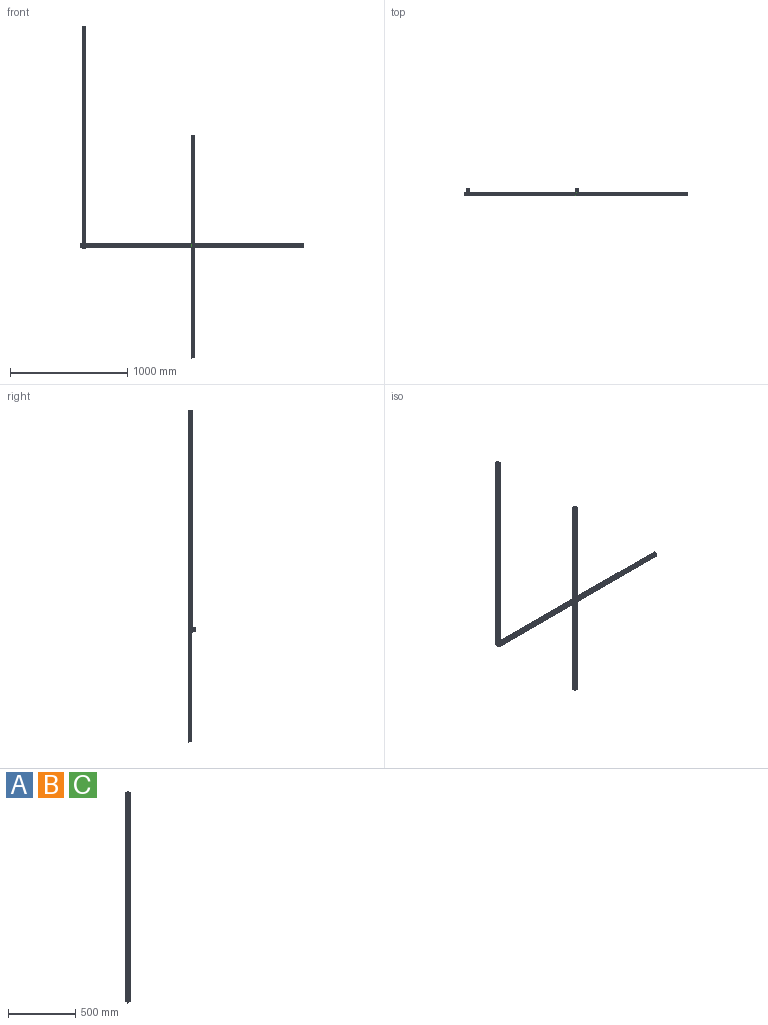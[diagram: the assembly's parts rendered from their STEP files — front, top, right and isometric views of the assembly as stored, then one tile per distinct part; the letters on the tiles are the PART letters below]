
ASSEMBLY  parts=3 mates=2
PART A: 242 faces, bbox 30x30x1900 mm
  f0: cylinder r=3.65mm len=1865.78mm, axis (0,0,1), area 6178.5mm2, adj f25,f39,f211,f240
  f1: cylinder r=3.65mm len=1865.78mm, axis (0,0,1), area 6178.5mm2, adj f31,f33,f212,f241
  f2: cylinder r=0.2mm len=1865.05mm, axis (0,0,1), area 193.9mm2, adj f3,f119,f212,f241
  f3: plane 1864.99x0.76mm, normal (-0.5,-0.87,0), area 1621.1mm2, adj f2,f4,f212,f241
  f4: cylinder r=0.2mm len=1864.7mm, axis (0,0,1), area 387.8mm2, adj f3,f123,f212,f241
  f5: plane 12.5x0.76mm, normal (0.5,-0.87,0), area 10.8mm2, adj f122,f124,f208,f212
  f6: cylinder r=0.2mm len=1865.05mm, axis (0,0,1), area 193.9mm2, adj f123,f125,f212,f241
  f7: cylinder r=0.2mm len=1865.05mm, axis (0,0,1), area 193.9mm2, adj f187,f189,f211,f240
  f8: plane 12.5x0.76mm, normal (0.5,0.87,0), area 10.8mm2, adj f188,f190,f208,f211
  f9: cylinder r=0.2mm len=1864.7mm, axis (0,0,1), area 387.8mm2, adj f10,f189,f211,f240
  f10: plane 1864.99x0.76mm, normal (-0.5,0.87,0), area 1621.1mm2, adj f9,f11,f211,f240
  f11: cylinder r=0.2mm len=1865.05mm, axis (0,0,1), area 193.9mm2, adj f10,f193,f211,f240
  f12: cylinder r=3.65mm len=1805.78mm, axis (0,0,1), area 5979.8mm2, adj f27,f29,f210,f239
  f13: cylinder r=3.65mm len=1805.78mm, axis (0,0,1), area 5979.8mm2, adj f35,f37,f209,f238
  f14: cylinder r=0.2mm len=1805.05mm, axis (0,0,1), area 187.7mm2, adj f15,f85,f210,f239
  f15: plane 1804.99x0.76mm, normal (0.87,-0.5,0), area 1569mm2, adj f14,f16,f210,f239
  f16: cylinder r=0.2mm len=1804.7mm, axis (0,0,1), area 375.3mm2, adj f15,f89,f210,f239
  f17: plane 42.5x0.76mm, normal (0.87,0.5,0), area 36.9mm2, adj f88,f90,f208,f210
  f18: cylinder r=0.2mm len=1805.05mm, axis (0,0,1), area 187.7mm2, adj f89,f91,f210,f239
  f19: cylinder r=0.2mm len=1805.05mm, axis (0,0,1), area 187.7mm2, adj f153,f155,f209,f238
  f20: plane 42.5x0.76mm, normal (-0.87,0.5,0), area 36.9mm2, adj f154,f156,f208,f209
  f21: cylinder r=0.2mm len=1804.7mm, axis (0,0,1), area 375.3mm2, adj f22,f155,f209,f238
  f22: plane 1804.99x0.76mm, normal (-0.87,-0.5,0), area 1569mm2, adj f21,f23,f209,f238
  f23: cylinder r=0.2mm len=1805.05mm, axis (0,0,1), area 187.7mm2, adj f22,f159,f209,f238
  f24: cylinder r=3.65mm len=12.89mm, axis (0,0,1), area 41.5mm2, adj f25,f39,f208,f211
  f25: plane 1900x1.54mm, normal (0.63,-0.78,0), area 3739.9mm2, adj f0,f24,f26,f208,f211,f217,f237,f240
  f26: cylinder r=5.5mm len=1900mm, axis (0,0,1), area 3691.1mm2, adj f25,f27,f208,f237
  f27: plane 1900x1.55mm, normal (-0.79,0.62,0), area 3752.3mm2, adj f12,f26,f28,f208,f210,f218,f237,f239
  f28: cylinder r=3.65mm len=42.89mm, axis (0,0,1), area 140.9mm2, adj f27,f29,f208,f210
  f29: plane 1900x1.55mm, normal (-0.79,-0.62,0), area 3752.3mm2, adj f12,f28,f30,f208,f210,f218,f237,f239
  f30: cylinder r=5.5mm len=1900mm, axis (0,0,1), area 3691.1mm2, adj f29,f31,f208,f237
  f31: plane 1900x1.54mm, normal (0.63,0.78,0), area 3739.9mm2, adj f1,f30,f32,f208,f212,f219,f237,f241
  f32: cylinder r=3.65mm len=12.89mm, axis (0,0,1), area 41.5mm2, adj f31,f33,f208,f212
  f33: plane 1900x1.54mm, normal (-0.63,0.78,0), area 3739.9mm2, adj f1,f32,f34,f208,f212,f219,f237,f241
  f34: cylinder r=5.5mm len=1900mm, axis (0,0,1), area 3691.1mm2, adj f33,f35,f208,f237
  f35: plane 1900x1.55mm, normal (0.79,-0.62,0), area 3752.3mm2, adj f13,f34,f36,f208,f209,f220,f237,f238
  f36: cylinder r=3.65mm len=42.89mm, axis (0,0,1), area 140.9mm2, adj f35,f37,f208,f209
  f37: plane 1900x1.55mm, normal (0.79,0.62,0), area 3752.3mm2, adj f13,f36,f38,f208,f209,f220,f237,f238
  f38: cylinder r=5.5mm len=1900mm, axis (0,0,1), area 3691.1mm2, adj f37,f39,f208,f237
  f39: plane 1900x1.54mm, normal (-0.63,-0.78,0), area 3739.9mm2, adj f0,f24,f38,f208,f211,f217,f237,f240
  f40: cylinder r=1mm len=1900mm, axis (0,0,1), area 2984.5mm2, adj f41,f47,f208,f237
  f41: plane 1900x2.2mm, normal (-1,0,0), area 4180mm2, adj f40,f42,f208,f237
  f42: cylinder r=1mm len=1900mm, axis (0,0,1), area 2984.5mm2, adj f41,f43,f208,f237
  f43: plane 1900x2.2mm, normal (0,1,0), area 4180mm2, adj f42,f44,f208,f237
  f44: cylinder r=1mm len=1900mm, axis (0,0,1), area 2984.5mm2, adj f43,f45,f208,f237
  f45: plane 1900x2.2mm, normal (1,0,0), area 4180mm2, adj f44,f46,f208,f237
  f46: cylinder r=1mm len=1900mm, axis (0,0,1), area 2984.5mm2, adj f45,f47,f208,f237
  f47: plane 1900x2.2mm, normal (0,-1,0), area 4180mm2, adj f40,f46,f208,f237
  f48: cylinder r=1mm len=1900mm, axis (0,0,1), area 2984.5mm2, adj f49,f55,f208,f237
  f49: plane 1900x2.2mm, normal (-1,0,0), area 4180mm2, adj f48,f50,f208,f237
  f50: cylinder r=1mm len=1900mm, axis (0,0,1), area 2984.5mm2, adj f49,f51,f208,f237
  f51: plane 1900x2.2mm, normal (0,1,0), area 4180mm2, adj f50,f52,f208,f237
  f52: cylinder r=1mm len=1900mm, axis (0,0,1), area 2984.5mm2, adj f51,f53,f208,f237
  f53: plane 1900x2.2mm, normal (1,0,0), area 4180mm2, adj f52,f54,f208,f237
  f54: cylinder r=1mm len=1900mm, axis (0,0,1), area 2984.5mm2, adj f53,f55,f208,f237
  f55: plane 1900x2.2mm, normal (0,-1,0), area 4180mm2, adj f48,f54,f208,f237
  f56: cylinder r=1mm len=1900mm, axis (0,0,1), area 2984.5mm2, adj f57,f63,f208,f237
  f57: plane 1900x2.2mm, normal (1,0,0), area 4180mm2, adj f56,f58,f208,f237
  f58: cylinder r=1mm len=1900mm, axis (0,0,1), area 2984.5mm2, adj f57,f59,f208,f237
  f59: plane 1900x2.2mm, normal (0,-1,0), area 4180mm2, adj f58,f60,f208,f237
  f60: cylinder r=1mm len=1900mm, axis (0,0,1), area 2984.5mm2, adj f59,f61,f208,f237
  f61: plane 1900x2.2mm, normal (-1,0,0), area 4180mm2, adj f60,f62,f208,f237
  f62: cylinder r=1mm len=1900mm, axis (0,0,1), area 2984.5mm2, adj f61,f63,f208,f237
  f63: plane 1900x2.2mm, normal (0,1,0), area 4180mm2, adj f56,f62,f208,f237
  f64: cylinder r=1mm len=1900mm, axis (0,0,1), area 2984.5mm2, adj f65,f71,f208,f237
  f65: plane 1900x2.2mm, normal (1,0,0), area 4180mm2, adj f64,f66,f208,f237
  f66: cylinder r=1mm len=1900mm, axis (0,0,1), area 2984.5mm2, adj f65,f67,f208,f237
  f67: plane 1900x2.2mm, normal (0,-1,0), area 4180mm2, adj f66,f68,f208,f237
  f68: cylinder r=1mm len=1900mm, axis (0,0,1), area 2984.5mm2, adj f67,f69,f208,f237
  f69: plane 1900x2.2mm, normal (-1,0,0), area 4180mm2, adj f68,f70,f208,f237
  f70: cylinder r=1mm len=1900mm, axis (0,0,1), area 2984.5mm2, adj f69,f71,f208,f237
  f71: plane 1900x2.2mm, normal (0,1,0), area 4180mm2, adj f64,f70,f208,f237
  f72: plane 1900x8.3mm, normal (1,0,0), area 15770mm2, adj f73,f207,f208,f237
  f73: cylinder r=0.2mm len=1900mm, axis (0,0,1), area 596.9mm2, adj f72,f74,f208,f237
  f74: plane 1900x0.3mm, normal (0,-1,0), area 570mm2, adj f73,f75,f208,f237
  f75: plane 1900x0.3mm, normal (1,0,0), area 570mm2, adj f74,f76,f208,f237
  f76: cylinder r=0.2mm len=1900mm, axis (0,0,1), area 596.9mm2, adj f75,f77,f208,f237
  f77: plane 1900x1mm, normal (0,-1,0), area 1900mm2, adj f76,f78,f208,f237
  f78: cylinder r=0.5mm len=1900mm, axis (0,0,1), area 1492.3mm2, adj f77,f79,f208,f237
  f79: plane 1900x3.25mm, normal (-1,0,0), area 6175mm2, adj f78,f80,f208,f237
  f80: cylinder r=0.5mm len=1900mm, axis (0,0,1), area 1492.3mm2, adj f79,f81,f208,f237
  f81: plane 1900x2.04mm, normal (0,-1,0), area 3881.8mm2, adj f80,f82,f208,f237
  f82: cylinder r=0.5mm len=1900mm, axis (0,0,1), area 745.6mm2, adj f81,f83,f208,f237
  f83: plane 1900x3.76mm, normal (0.71,-0.71,0), area 10089.4mm2, adj f82,f84,f208,f237
  f84: cylinder r=0.5mm len=1900mm, axis (0,0,1), area 746.7mm2, adj f83,f85,f208,f237
  f85: plane 1900x3.04mm, normal (1,0,0), area 5771.4mm2, adj f14,f84,f86,f208,f210,f221,f237,f239
  f86: cylinder r=0.2mm len=42.53mm, axis (0,0,1), area 4.4mm2, adj f85,f87,f208,f210
  f87: plane 42.5x0.76mm, normal (0.87,-0.5,0), area 36.9mm2, adj f86,f88,f208,f210
  f88: cylinder r=0.2mm len=42.35mm, axis (0,0,1), area 8.8mm2, adj f17,f87,f208,f210
  f89: plane 1804.99x0.76mm, normal (0.87,0.5,0), area 1569mm2, adj f16,f18,f210,f239
  f90: cylinder r=0.2mm len=42.53mm, axis (0,0,1), area 4.4mm2, adj f17,f91,f208,f210
  f91: plane 1900x3.04mm, normal (1,0,0), area 5771.4mm2, adj f18,f90,f92,f208,f210,f224,f237,f239
  f92: cylinder r=0.5mm len=1900mm, axis (0,0,1), area 746.7mm2, adj f91,f93,f208,f237
  f93: plane 1900x3.76mm, normal (0.71,0.71,0), area 10089.4mm2, adj f92,f94,f208,f237
  f94: cylinder r=0.5mm len=1900mm, axis (0,0,1), area 745.6mm2, adj f93,f95,f208,f237
  f95: plane 1900x2.04mm, normal (0,1,0), area 3881.8mm2, adj f94,f96,f208,f237
  f96: cylinder r=0.5mm len=1900mm, axis (0,0,1), area 1492.3mm2, adj f95,f97,f208,f237
  f97: plane 1900x3.25mm, normal (-1,0,0), area 6175mm2, adj f96,f98,f208,f237
  f98: cylinder r=0.5mm len=1900mm, axis (0,0,1), area 1492.3mm2, adj f97,f99,f208,f237
  f99: plane 1900x1mm, normal (0,1,0), area 1900mm2, adj f98,f100,f208,f237
  f100: cylinder r=0.2mm len=1900mm, axis (0,0,1), area 596.9mm2, adj f99,f101,f208,f237
  f101: plane 1900x0.3mm, normal (1,0,0), area 570mm2, adj f100,f102,f208,f237
  f102: plane 1900x0.3mm, normal (0,1,0), area 570mm2, adj f101,f103,f208,f237
  f103: cylinder r=0.2mm len=1900mm, axis (0,0,1), area 596.9mm2, adj f102,f104,f208,f237
  f104: plane 1900x8.3mm, normal (1,0,0), area 15770mm2, adj f103,f105,f208,f237
  f105: cylinder r=2mm len=1900mm, axis (0,0,1), area 5969mm2, adj f104,f106,f208,f237
  f106: plane 1900x8.3mm, normal (0,-1,0), area 15770mm2, adj f105,f107,f208,f237
  f107: cylinder r=0.2mm len=1900mm, axis (0,0,1), area 596.9mm2, adj f106,f108,f208,f237
  f108: plane 1900x0.3mm, normal (-1,0,0), area 570mm2, adj f107,f109,f208,f237
  f109: plane 1900x0.3mm, normal (0,-1,0), area 570mm2, adj f108,f110,f208,f237
  f110: cylinder r=0.2mm len=1900mm, axis (0,0,1), area 596.9mm2, adj f109,f111,f208,f237
  f111: plane 1900x1mm, normal (-1,0,0), area 1900mm2, adj f110,f112,f208,f237
  f112: cylinder r=0.5mm len=1900mm, axis (0,0,1), area 1492.3mm2, adj f111,f113,f208,f237
  f113: plane 1900x3.25mm, normal (0,1,0), area 6175mm2, adj f112,f114,f208,f237
  f114: cylinder r=0.5mm len=1900mm, axis (0,0,1), area 1492.3mm2, adj f113,f115,f208,f237
  f115: plane 1900x2.04mm, normal (-1,0,0), area 3881.8mm2, adj f114,f116,f208,f237
  f116: cylinder r=0.5mm len=1900mm, axis (0,0,1), area 745.6mm2, adj f115,f117,f208,f237
  f117: plane 1900x3.76mm, normal (-0.71,-0.71,0), area 10089.4mm2, adj f116,f118,f208,f237
  f118: cylinder r=0.5mm len=1900mm, axis (0,0,1), area 746.7mm2, adj f117,f119,f208,f237
  f119: plane 1900x3.04mm, normal (0,-1,0), area 5771.4mm2, adj f2,f118,f120,f208,f212,f225,f237,f241
  f120: cylinder r=0.2mm len=12.53mm, axis (0,0,1), area 1.3mm2, adj f119,f121,f208,f212
  f121: plane 12.5x0.76mm, normal (-0.5,-0.87,0), area 10.8mm2, adj f120,f122,f208,f212
  f122: cylinder r=0.2mm len=12.35mm, axis (0,0,1), area 2.6mm2, adj f5,f121,f208,f212
  f123: plane 1864.99x0.76mm, normal (0.5,-0.87,0), area 1621.1mm2, adj f4,f6,f212,f241
  f124: cylinder r=0.2mm len=12.53mm, axis (0,0,1), area 1.3mm2, adj f5,f125,f208,f212
  f125: plane 1900x3.04mm, normal (0,-1,0), area 5771.4mm2, adj f6,f124,f126,f208,f212,f228,f237,f241
  f126: cylinder r=0.5mm len=1900mm, axis (0,0,1), area 746.7mm2, adj f125,f127,f208,f237
  f127: plane 1900x3.76mm, normal (0.71,-0.71,0), area 10089.4mm2, adj f126,f128,f208,f237
  f128: cylinder r=0.5mm len=1900mm, axis (0,0,1), area 745.6mm2, adj f127,f129,f208,f237
  f129: plane 1900x2.04mm, normal (1,0,0), area 3881.8mm2, adj f128,f130,f208,f237
  f130: cylinder r=0.5mm len=1900mm, axis (0,0,1), area 1492.3mm2, adj f129,f131,f208,f237
  f131: plane 1900x3.25mm, normal (0,1,0), area 6175mm2, adj f130,f132,f208,f237
  f132: cylinder r=0.5mm len=1900mm, axis (0,0,1), area 1492.3mm2, adj f131,f133,f208,f237
  f133: plane 1900x1mm, normal (1,0,0), area 1900mm2, adj f132,f134,f208,f237
  f134: cylinder r=0.2mm len=1900mm, axis (0,0,1), area 596.9mm2, adj f133,f135,f208,f237
  f135: plane 1900x0.3mm, normal (0,-1,0), area 570mm2, adj f134,f136,f208,f237
  f136: plane 1900x0.3mm, normal (1,0,0), area 570mm2, adj f135,f137,f208,f237
  f137: cylinder r=0.2mm len=1900mm, axis (0,0,1), area 596.9mm2, adj f136,f138,f208,f237
  f138: plane 1900x8.3mm, normal (0,-1,0), area 15770mm2, adj f137,f139,f208,f237
  f139: cylinder r=2mm len=1900mm, axis (0,0,1), area 5969mm2, adj f138,f140,f208,f237
  f140: plane 1900x8.3mm, normal (-1,0,0), area 15770mm2, adj f139,f141,f208,f237
  f141: cylinder r=0.2mm len=1900mm, axis (0,0,1), area 596.9mm2, adj f140,f142,f208,f237
  f142: plane 1900x0.3mm, normal (0,1,0), area 570mm2, adj f141,f143,f208,f237
  f143: plane 1900x0.3mm, normal (-1,0,0), area 570mm2, adj f142,f144,f208,f237
  f144: cylinder r=0.2mm len=1900mm, axis (0,0,1), area 596.9mm2, adj f143,f145,f208,f237
  f145: plane 1900x1mm, normal (0,1,0), area 1900mm2, adj f144,f146,f208,f237
  f146: cylinder r=0.5mm len=1900mm, axis (0,0,1), area 1492.3mm2, adj f145,f147,f208,f237
  f147: plane 1900x3.25mm, normal (1,0,0), area 6175mm2, adj f146,f148,f208,f237
  f148: cylinder r=0.5mm len=1900mm, axis (0,0,1), area 1492.3mm2, adj f147,f149,f208,f237
  f149: plane 1900x2.04mm, normal (0,1,0), area 3881.8mm2, adj f148,f150,f208,f237
  f150: cylinder r=0.5mm len=1900mm, axis (0,0,1), area 745.6mm2, adj f149,f151,f208,f237
  f151: plane 1900x3.76mm, normal (-0.71,0.71,0), area 10089.4mm2, adj f150,f152,f208,f237
  f152: cylinder r=0.5mm len=1900mm, axis (0,0,1), area 746.7mm2, adj f151,f153,f208,f237
  f153: plane 1900x3.04mm, normal (-1,0,0), area 5771.4mm2, adj f19,f152,f154,f208,f209,f229,f237,f238
  f154: cylinder r=0.2mm len=42.53mm, axis (0,0,1), area 4.4mm2, adj f20,f153,f208,f209
  f155: plane 1804.99x0.76mm, normal (-0.87,0.5,0), area 1569mm2, adj f19,f21,f209,f238
  f156: cylinder r=0.2mm len=42.35mm, axis (0,0,1), area 8.8mm2, adj f20,f157,f208,f209
  f157: plane 42.5x0.76mm, normal (-0.87,-0.5,0), area 36.9mm2, adj f156,f158,f208,f209
  f158: cylinder r=0.2mm len=42.53mm, axis (0,0,1), area 4.4mm2, adj f157,f159,f208,f209
  f159: plane 1900x3.04mm, normal (-1,0,0), area 5771.4mm2, adj f23,f158,f160,f208,f209,f232,f237,f238
  f160: cylinder r=0.5mm len=1900mm, axis (0,0,1), area 746.7mm2, adj f159,f161,f208,f237
  f161: plane 1900x3.76mm, normal (-0.71,-0.71,0), area 10089.4mm2, adj f160,f162,f208,f237
  f162: cylinder r=0.5mm len=1900mm, axis (0,0,1), area 745.6mm2, adj f161,f163,f208,f237
  f163: plane 1900x2.04mm, normal (0,-1,0), area 3881.8mm2, adj f162,f164,f208,f237
  f164: cylinder r=0.5mm len=1900mm, axis (0,0,1), area 1492.3mm2, adj f163,f165,f208,f237
  f165: plane 1900x3.25mm, normal (1,0,0), area 6175mm2, adj f164,f166,f208,f237
  f166: cylinder r=0.5mm len=1900mm, axis (0,0,1), area 1492.3mm2, adj f165,f167,f208,f237
  f167: plane 1900x1mm, normal (0,-1,0), area 1900mm2, adj f166,f168,f208,f237
  f168: cylinder r=0.2mm len=1900mm, axis (0,0,1), area 596.9mm2, adj f167,f169,f208,f237
  f169: plane 1900x0.3mm, normal (-1,0,0), area 570mm2, adj f168,f170,f208,f237
  f170: plane 1900x0.3mm, normal (0,-1,0), area 570mm2, adj f169,f171,f208,f237
  f171: cylinder r=0.2mm len=1900mm, axis (0,0,1), area 596.9mm2, adj f170,f172,f208,f237
  f172: plane 1900x8.3mm, normal (-1,0,0), area 15770mm2, adj f171,f173,f208,f237
  f173: cylinder r=2mm len=1900mm, axis (0,0,1), area 5969mm2, adj f172,f174,f208,f237
  f174: plane 1900x8.3mm, normal (0,1,0), area 15770mm2, adj f173,f175,f208,f237
  f175: cylinder r=0.2mm len=1900mm, axis (0,0,1), area 596.9mm2, adj f174,f176,f208,f237
  f176: plane 1900x0.3mm, normal (1,0,0), area 570mm2, adj f175,f177,f208,f237
  f177: plane 1900x0.3mm, normal (0,1,0), area 570mm2, adj f176,f178,f208,f237
  f178: cylinder r=0.2mm len=1900mm, axis (0,0,1), area 596.9mm2, adj f177,f179,f208,f237
  f179: plane 1900x1mm, normal (1,0,0), area 1900mm2, adj f178,f180,f208,f237
  f180: cylinder r=0.5mm len=1900mm, axis (0,0,1), area 1492.3mm2, adj f179,f181,f208,f237
  f181: plane 1900x3.25mm, normal (0,-1,0), area 6175mm2, adj f180,f182,f208,f237
  f182: cylinder r=0.5mm len=1900mm, axis (0,0,1), area 1492.3mm2, adj f181,f183,f208,f237
  f183: plane 1900x2.04mm, normal (1,0,0), area 3881.8mm2, adj f182,f184,f208,f237
  f184: cylinder r=0.5mm len=1900mm, axis (0,0,1), area 745.6mm2, adj f183,f185,f208,f237
  f185: plane 1900x3.76mm, normal (0.71,0.71,0), area 10089.4mm2, adj f184,f186,f208,f237
  f186: cylinder r=0.5mm len=1900mm, axis (0,0,1), area 746.7mm2, adj f185,f187,f208,f237
  f187: plane 1900x3.04mm, normal (0,1,0), area 5771.4mm2, adj f7,f186,f188,f208,f211,f233,f237,f240
  f188: cylinder r=0.2mm len=12.53mm, axis (0,0,1), area 1.3mm2, adj f8,f187,f208,f211
  f189: plane 1864.99x0.76mm, normal (0.5,0.87,0), area 1621.1mm2, adj f7,f9,f211,f240
  f190: cylinder r=0.2mm len=12.35mm, axis (0,0,1), area 2.6mm2, adj f8,f191,f208,f211
  f191: plane 12.5x0.76mm, normal (-0.5,0.87,0), area 10.8mm2, adj f190,f192,f208,f211
  f192: cylinder r=0.2mm len=12.53mm, axis (0,0,1), area 1.3mm2, adj f191,f193,f208,f211
  f193: plane 1900x3.04mm, normal (0,1,0), area 5771.4mm2, adj f11,f192,f194,f208,f211,f236,f237,f240
  f194: cylinder r=0.5mm len=1900mm, axis (0,0,1), area 746.7mm2, adj f193,f195,f208,f237
  f195: plane 1900x3.76mm, normal (-0.71,0.71,0), area 10089.4mm2, adj f194,f196,f208,f237
  f196: cylinder r=0.5mm len=1900mm, axis (0,0,1), area 745.6mm2, adj f195,f197,f208,f237
  f197: plane 1900x2.04mm, normal (-1,0,0), area 3881.8mm2, adj f196,f198,f208,f237
  f198: cylinder r=0.5mm len=1900mm, axis (0,0,1), area 1492.3mm2, adj f197,f199,f208,f237
  f199: plane 1900x3.25mm, normal (0,-1,0), area 6175mm2, adj f198,f200,f208,f237
  f200: cylinder r=0.5mm len=1900mm, axis (0,0,1), area 1492.3mm2, adj f199,f201,f208,f237
  f201: plane 1900x1mm, normal (-1,0,0), area 1900mm2, adj f200,f202,f208,f237
  f202: cylinder r=0.2mm len=1900mm, axis (0,0,1), area 596.9mm2, adj f201,f203,f208,f237
  f203: plane 1900x0.3mm, normal (0,1,0), area 570mm2, adj f202,f204,f208,f237
  f204: plane 1900x0.3mm, normal (-1,0,0), area 570mm2, adj f203,f205,f208,f237
  f205: cylinder r=0.2mm len=1900mm, axis (0,0,1), area 596.9mm2, adj f204,f206,f208,f237
  f206: plane 1900x8.3mm, normal (0,1,0), area 15770mm2, adj f205,f207,f208,f237
  f207: cylinder r=2mm len=1900mm, axis (0,0,1), area 5969mm2, adj f72,f206,f208,f237
  f208: plane 30x30mm, normal (0,0,-1), area 313.9mm2, adj f5,f8,f17,f20,f24,f25,f26,f27
  f209: cylinder r=2.65mm len=5.3mm, axis (1,0,0), area 37.4mm2, adj f13,f19,f20,f21,f22,f23,f35,f36
  f210: cylinder r=2.65mm len=5.3mm, axis (1,0,0), area 37.4mm2, adj f12,f14,f15,f16,f17,f18,f27,f28
  f211: cylinder r=2.65mm len=5.3mm, axis (0,-1,0), area 37.2mm2, adj f0,f7,f8,f9,f10,f11,f24,f25
  f212: cylinder r=2.65mm len=5.3mm, axis (0,-1,0), area 37.2mm2, adj f1,f2,f3,f4,f5,f6,f31,f32
  f213: plane 12.5x0.76mm, normal (0.5,-0.87,0), area 10.8mm2, adj f227,f228,f237,f241
  f214: plane 12.5x0.76mm, normal (0.5,0.87,0), area 10.8mm2, adj f233,f234,f237,f240
  f215: plane 42.5x0.76mm, normal (0.87,0.5,0), area 36.9mm2, adj f223,f224,f237,f239
  f216: plane 42.5x0.76mm, normal (-0.87,0.5,0), area 36.9mm2, adj f229,f230,f237,f238
  f217: cylinder r=3.65mm len=12.89mm, axis (0,0,-1), area 41.5mm2, adj f25,f39,f237,f240
  f218: cylinder r=3.65mm len=42.89mm, axis (0,0,-1), area 140.9mm2, adj f27,f29,f237,f239
  f219: cylinder r=3.65mm len=12.89mm, axis (0,0,-1), area 41.5mm2, adj f31,f33,f237,f241
  f220: cylinder r=3.65mm len=42.89mm, axis (0,0,-1), area 140.9mm2, adj f35,f37,f237,f238
  f221: cylinder r=0.2mm len=42.53mm, axis (0,0,-1), area 4.4mm2, adj f85,f222,f237,f239
  f222: plane 42.5x0.76mm, normal (0.87,-0.5,0), area 36.9mm2, adj f221,f223,f237,f239
  f223: cylinder r=0.2mm len=42.35mm, axis (0,0,-1), area 8.8mm2, adj f215,f222,f237,f239
  f224: cylinder r=0.2mm len=42.53mm, axis (0,0,-1), area 4.4mm2, adj f91,f215,f237,f239
  f225: cylinder r=0.2mm len=12.53mm, axis (0,0,-1), area 1.3mm2, adj f119,f226,f237,f241
  f226: plane 12.5x0.76mm, normal (-0.5,-0.87,0), area 10.8mm2, adj f225,f227,f237,f241
  f227: cylinder r=0.2mm len=12.35mm, axis (0,0,-1), area 2.6mm2, adj f213,f226,f237,f241
  f228: cylinder r=0.2mm len=12.53mm, axis (0,0,-1), area 1.3mm2, adj f125,f213,f237,f241
  f229: cylinder r=0.2mm len=42.53mm, axis (0,0,-1), area 4.4mm2, adj f153,f216,f237,f238
  f230: cylinder r=0.2mm len=42.35mm, axis (0,0,-1), area 8.8mm2, adj f216,f231,f237,f238
  f231: plane 42.5x0.76mm, normal (-0.87,-0.5,0), area 36.9mm2, adj f230,f232,f237,f238
  f232: cylinder r=0.2mm len=42.53mm, axis (0,0,-1), area 4.4mm2, adj f159,f231,f237,f238
  f233: cylinder r=0.2mm len=12.53mm, axis (0,0,-1), area 1.3mm2, adj f187,f214,f237,f240
  f234: cylinder r=0.2mm len=12.35mm, axis (0,0,-1), area 2.6mm2, adj f214,f235,f237,f240
  f235: plane 12.5x0.76mm, normal (-0.5,0.87,0), area 10.8mm2, adj f234,f236,f237,f240
  f236: cylinder r=0.2mm len=12.53mm, axis (0,0,-1), area 1.3mm2, adj f193,f235,f237,f240
  f237: plane 30x30mm, normal (0,0,1), area 313.9mm2, adj f25,f26,f27,f29,f30,f31,f33,f34
  f238: cylinder r=2.65mm len=5.3mm, axis (1,0,0), area 37.4mm2, adj f13,f19,f21,f22,f23,f35,f37,f153
  f239: cylinder r=2.65mm len=5.3mm, axis (1,0,0), area 37.4mm2, adj f12,f14,f15,f16,f18,f27,f29,f85
  f240: cylinder r=2.65mm len=5.3mm, axis (0,-1,0), area 37.2mm2, adj f0,f7,f9,f10,f11,f25,f39,f187
  f241: cylinder r=2.65mm len=5.3mm, axis (0,-1,0), area 37.2mm2, adj f1,f2,f3,f4,f6,f31,f33,f119
PART B: same geometry as A
PART C: same geometry as A
PLACE A t=(2046.42,265.7,-2695.17)mm
PLACE B t=(1116.42,265.7,-1762.17)mm
PLACE C rot(axis=(0,1,0),90deg) t=(1082.87,235.7,-1741.02)mm
MATE planar B.f138 <-> C.f206  axis (0,-1,0) through (1102.87,235.7,-812.17)mm
MATE planar A.f138 <-> C.f206  axis (0,-1,0) through (2032.87,235.7,-1745.17)mm
